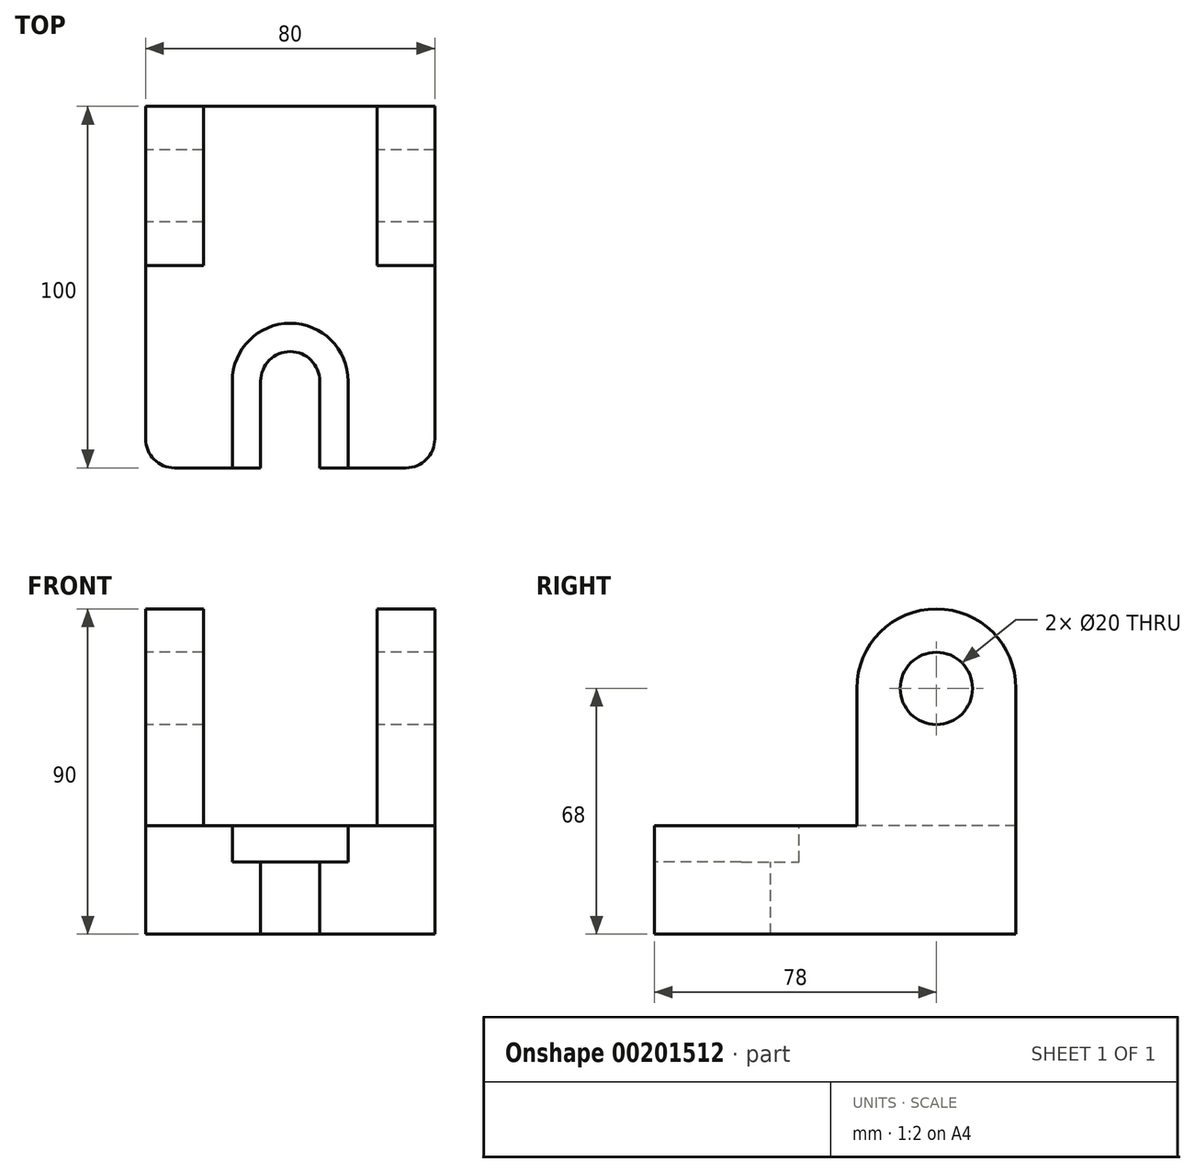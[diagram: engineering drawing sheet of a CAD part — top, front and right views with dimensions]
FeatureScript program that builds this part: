
annotation { "Feature Type Name" : "Feature", "Feature Type Description" : "" }
export const myFeature = defineFeature(function(context is Context, id is Id, definition is map)
    precondition{}
    {
        {
            var Q0;
            Q0=qCreatedBy(makeId("Right.planeOp"),FACE);
            var sketch = newSketch(context, id + "F0", { "sketchPlane" : qUnion([Q0])});
            skLineSegment(sketch, "E0", {"start": v(0, 0) * mm, "end": v(-100, 0) * mm});
            skLineSegment(sketch, "E1", {"start": v(-100, 0) * mm, "end": v(-100, 30) * mm});
            skLineSegment(sketch, "E2", {"start": v(-100, 30) * mm, "end": v(-44, 30) * mm});
            skLineSegment(sketch, "E3", {"start": v(-44, 30) * mm, "end": v(-44, 68) * mm});
            skArc(sketch, "E4", {"start": v(-44, 68) * mm, "mid": v(-22, 90) * mm, "end": v(0, 68) * mm});
            skLineSegment(sketch, "E5", {"start": v(0, 68) * mm, "end": v(0, 0) * mm});
            skCircle(sketch, "E6", {"center": v(-22, 68) * mm, "radius": 10 * mm});
            skSolve(sketch);
        }
        {
            var Q0;
            Q0=qSketchRegion(id+"F0",true);
            extrude(context, id + "F1", {"entities" : qUnion([Q0]), "endBound" : BoundingType.SYMMETRIC, "depth" : 80 * mm});
        }
        {
            var Q0;
            Q0=makeQuery(id+"F1.opExtrude","SWEPT_FACE",FACE,{"disambiguationData":[OSD([sQuery(id+"F0.wireOp",EDGE,"E3")])]});
            var sketch = newSketch(context, id + "F2", { "sketchPlane" : qUnion([Q0])});
            skLineSegment(sketch, "E7", {"start": v(-24, 30) * mm, "end": v(-24, 90) * mm});
            skLineSegment(sketch, "E8", {"start": v(-24, 90) * mm, "end": v(24, 90) * mm});
            skLineSegment(sketch, "E9", {"start": v(24, 90) * mm, "end": v(24, 30) * mm});
            skSolve(sketch);
        }
        {
            var Q0;
            {var subQ0=sQuery(id+"F2.wireOp",EDGE,"E7");var subQ1=sQuery(id+"F0.wireOp",EDGE,"E3");var subQ2=makeQuery(id+"F1.opExtrude","SWEPT_EDGE",EDGE,{"disambiguationData":[OSD([sQuery(id+"F0.wireOp",EDGE,"E2"),subQ1])]});var subQ3=makeQuery(id+"F2.imprint","INTERSECT",VERTEX,{"derivedFrom":[subQ2,subQ0]});Q0=makeQuery(id+"F2.imprint","IMPRINT",FACE,{"disambiguationData":[TD([[makeQuery(id+"F2.imprint","IMPRINT",EDGE,{"disambiguationData":[TD([[subQ3,-1.0]])],"derivedFrom":subQ0}),-1.0]])]});}
            var Q1;
            {var subQ0=sQuery(id+"F2.wireOp",EDGE,"E8");Q1=makeQuery(id+"F2.imprint","IMPRINT",FACE,{"disambiguationData":[TD([[makeQuery(id+"F2.imprint","IMPRINT",EDGE,{"derivedFrom":subQ0}),-1.0]])]});}
            extrude(context, id + "F3", {"entities" : qUnion([Q0, Q1]), "operationType" : NewBodyOperationType.REMOVE, "endBound" : BoundingType.THROUGH_ALL, "oppositeDirection" : true, "depth" : 25 * mm});
        }
        {
            var Q0;
            {var subQ0=sQuery(id+"F0.wireOp",EDGE,"E2");Q0=makeQuery(id+"F3.boolean.opBoolean","MERGE",FACE,{"derivedFrom":[makeQuery(id+"F1.opExtrude","SWEPT_FACE",FACE,{"disambiguationData":[OSD([subQ0])]}),makeQuery(id+"F3.opExtrude","SWEPT_FACE",FACE,{"disambiguationData":[OSD([subQ0,sQuery(id+"F0.wireOp",EDGE,"E3")])]})]});}
            var sketch = newSketch(context, id + "F4", { "sketchPlane" : qUnion([Q0])});
            skLineSegment(sketch, "E10", {"start": v(-16, -100) * mm, "end": v(-16, -76) * mm});
            skArc(sketch, "E11", {"start": v(-16, -76) * mm, "mid": v(0, -60) * mm, "end": v(16, -76) * mm});
            skLineSegment(sketch, "E12", {"start": v(16, -76) * mm, "end": v(16, -100) * mm});
            skLineSegment(sketch, "E13.0", {"start": v(8.16, -76) * mm, "end": v(8.16, -100) * mm});
            skArc(sketch, "E13.1", {"start": v(-8.16, -76) * mm, "mid": v(0, -67.84) * mm, "end": v(8.16, -76) * mm});
            skLineSegment(sketch, "E13.2", {"start": v(-8.16, -100) * mm, "end": v(-8.16, -76) * mm});
            skSolve(sketch);
        }
        {
            var Q0;
            {var subQ0=sQuery(id+"F4.wireOp",EDGE,"E13.0");Q0=makeQuery(id+"F4.imprint","IMPRINT",FACE,{"disambiguationData":[TD([[makeQuery(id+"F4.imprint","IMPRINT",EDGE,{"derivedFrom":subQ0}),-1.0]])]});}
            extrude(context, id + "F5", {"entities" : qUnion([Q0]), "operationType" : NewBodyOperationType.REMOVE, "endBound" : BoundingType.THROUGH_ALL, "oppositeDirection" : true, "depth" : 25 * mm});
        }
        {
            var Q0;
            {var subQ2=sQuery(id+"F4.wireOp",EDGE,"E10");Q0=makeQuery(id+"F4.imprint","IMPRINT",FACE,{"disambiguationData":[TD([[makeQuery(id+"F4.imprint","IMPRINT",EDGE,{"derivedFrom":subQ2}),-1.0]])]});}
            extrude(context, id + "F6", {"entities" : qUnion([Q0]), "operationType" : NewBodyOperationType.REMOVE, "oppositeDirection" : true, "depth" : 10 * mm});
        }
        {
            var Q0;
            Q0=makeQuery(id+"F1.opExtrude","CAP_EDGE",EDGE,{"disambiguationData":[OSD([sQuery(id+"F0.wireOp",EDGE,"E1")])],"isStart":true});
            var Q1;
            Q1=makeQuery(id+"F1.opExtrude","CAP_EDGE",EDGE,{"disambiguationData":[OSD([sQuery(id+"F0.wireOp",EDGE,"E1")])],"isStart":false});
            fillet(context, id + "F7", {"entities" : qUnion([Q0, Q1]), "radius" : 8 * mm, "tangentPropagation" : true, "allowEdgeOverflow" : false});
        }
    });
